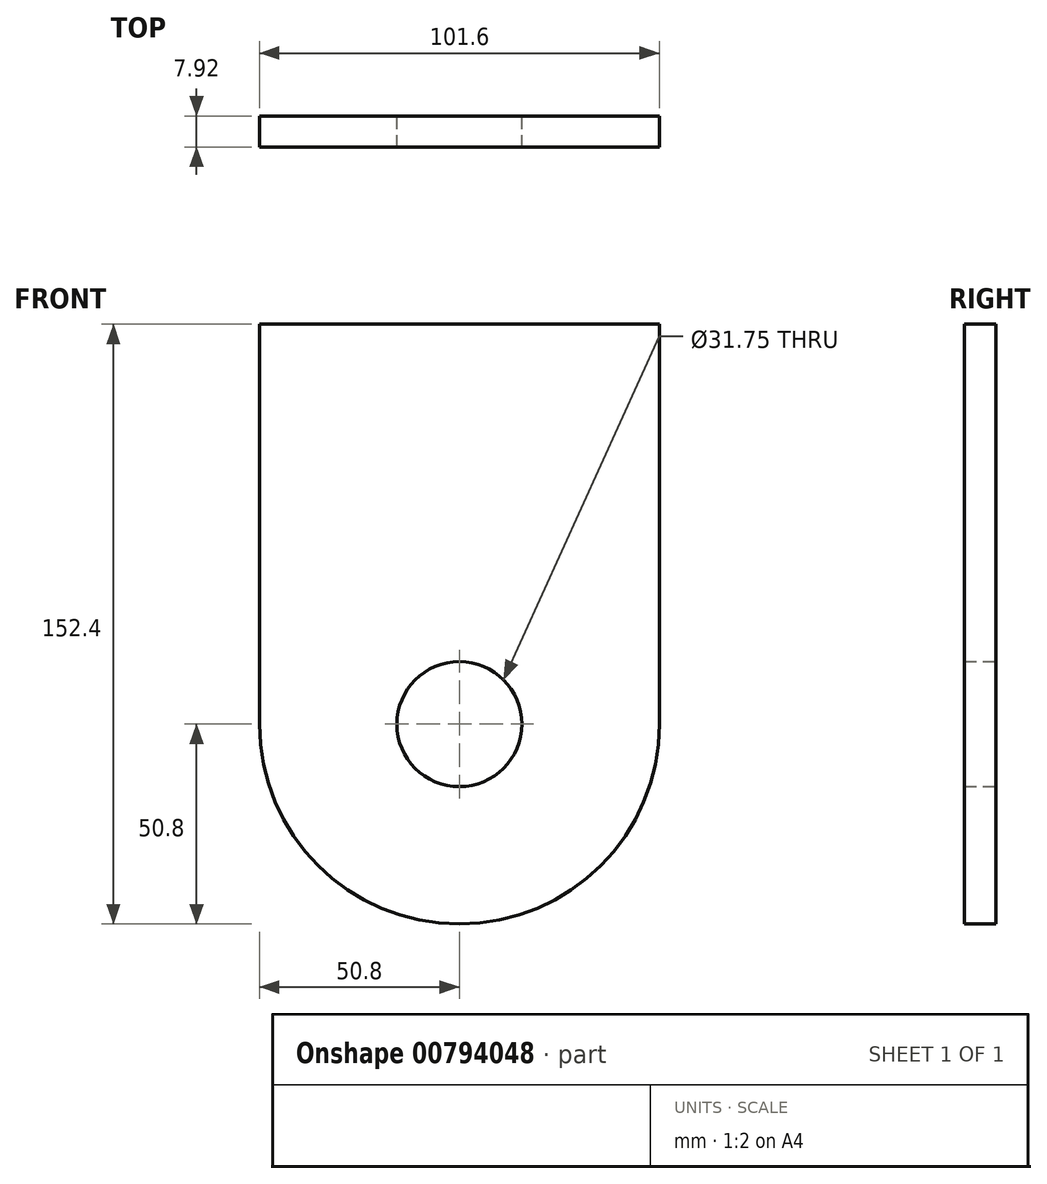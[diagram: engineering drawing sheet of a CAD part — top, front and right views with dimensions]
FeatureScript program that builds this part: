
annotation { "Feature Type Name" : "Feature", "Feature Type Description" : "" }
export const myFeature = defineFeature(function(context is Context, id is Id, definition is map)
    precondition{}
    {
        {
            var Q0;
            Q0=qCreatedBy(makeId("Front.planeOp"),FACE);
            var sketch = newSketch(context, id + "F0", { "sketchPlane" : qUnion([Q0])});
            skCircle(sketch, "E0", {"center": v(0, 0) * mm, "radius": 15.88 * mm});
            skCircle(sketch, "E1", {"center": v(0, 0) * mm, "radius": 50.8 * mm});
            skLineSegment(sketch, "E2.bottom", {"start": v(50.8, 101.6) * mm, "end": v(-50.8, 101.6) * mm});
            skLineSegment(sketch, "E2.left", {"start": v(50.8, 101.6) * mm, "end": v(50.8, 0) * mm});
            skLineSegment(sketch, "E2.right", {"start": v(-50.8, 101.6) * mm, "end": v(-50.8, 0) * mm});
            skPoint(sketch, "E2.top.end.orphan", {"position": v(-50.8, -101.6) * mm});
            skPoint(sketch, "E2.top.start.orphan", {"position": v(50.8, -101.6) * mm});
            skSolve(sketch);
        }
        {
            var Q0;
            Q0 = qSketchRegion(id + "F0", true);
            extrude(context, id + "F1", {"entities" : qUnion([Q0]), "depth" : 7.92 * mm, "offsetDistance" : 25.4 * mm});
        }
    });
